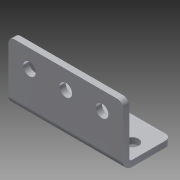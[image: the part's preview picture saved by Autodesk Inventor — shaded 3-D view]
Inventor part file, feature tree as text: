
AUTODESK INVENTOR PART (.ipt)
format: ipt  version: 2013 (Build 170138000, 138)  size: 195,072 bytes
history: native  units: in
note: dims shown in document units (in); Inventor stores cm internally (conversion verified against a paired STEP export)
features: sheet_metal_op x4, other x4, sketch x3, chamfer x1
ambient origin geometry x8: Origin, YZ Plane, XZ Plane, XY Plane, X Axis, Y Axis, Z Axis, Center Point
bodies: Solid1 (feature_tree)
feature tree (12):
  sheet_metal_op  "Face1"
  sheet_metal_op  "Flange1"
  chamfer  "Corner Round1"
  sketch  "Sketch1"  dims[d0=2.375in]
  other  "Plate1"
  sketch  "Sketch2"  dims[d1=1.0in]
  other  "Plate2"
  sheet_metal_op  "Bend1"
  sheet_metal_op  "Corner1"
  sketch  "Sketch3"  dims[d2=0.26in d3=1.75in d4=0.125in d5=0.125in d6=0.0625in d7=0.25in d8=0.125in d9=1.25in d10=90.0deg d11=0.05in d12=0.5in d13=0.125in d14=0.125in d15=1.5in d17=0.26in d19=0.875in d20=0.125in d21=0.0in d22=0.125in d23=0.3125in]
  other  "Cut1"
  other  "Definition1"
